# Revit family: DSP_A3-Double-Louvre-Door-2380
name_source: partatom
category: Doors
revit_build: Autodesk Revit 2016 (Build: 20150220_1215(x64)
units: mm (PartAtom-declared; Revit-internal decimal feet)

## family parameters
Always vertical = Yes
Cut with Voids When Loaded = No
Host = Wall
Room Calculation Point = No
Shared = No

## types (4) — shared parameters
Construction Type = Timber
Frame Width = 33 mm  [stored 0.108268 ft]
Function = Interior
Manufacturer = Swartland
Material Door Frame = Default Timber Door Frame
Material Door Panel = Default Timber Door Panel
Material Glass = Glass
Model = Winsters
Model Type = Double Door
URL = http://www.swartland.co.za
Wall Closure = By host
zero-valued in all types: Thickness

## per-type parameters (varying)
| type | Height | Manufacturer Code Frame | Manufacturer Code Panel | Rough Height | Rough Width | Width |
| 1612w X 2125 | 2125 mm  [stored 6.97178 ft] |  |  | 2032 mm | 1610 mm | 1676 mm  [stored 5.49869 ft] |
| 1210w X 2125 | 2125 mm  [stored 6.97178 ft] | 1210 N/S | PD6-1210 | 2032 mm | 1210 mm | 1276 mm  [stored 4.18635 ft] |
| 1210w X 2465 | 2465 mm  [stored 8.08727 ft] | 1210 N/S | PD6-1210 | 2372 mm  [stored 7.78215 ft] | 1210 mm | 1276 mm  [stored 4.18635 ft] |
| 1612w X 2465 | 2432 mm |  |  | 2339 mm | 1610 mm | 1676 mm  [stored 5.49869 ft] |

note: [stored X ft] marks values corroborated as IEEE doubles in the binary element streams (Revit-internal decimal feet)

## geometry (parser evidence)
native form markers: Sweep x4
no freeform markers — native parametric forms only
